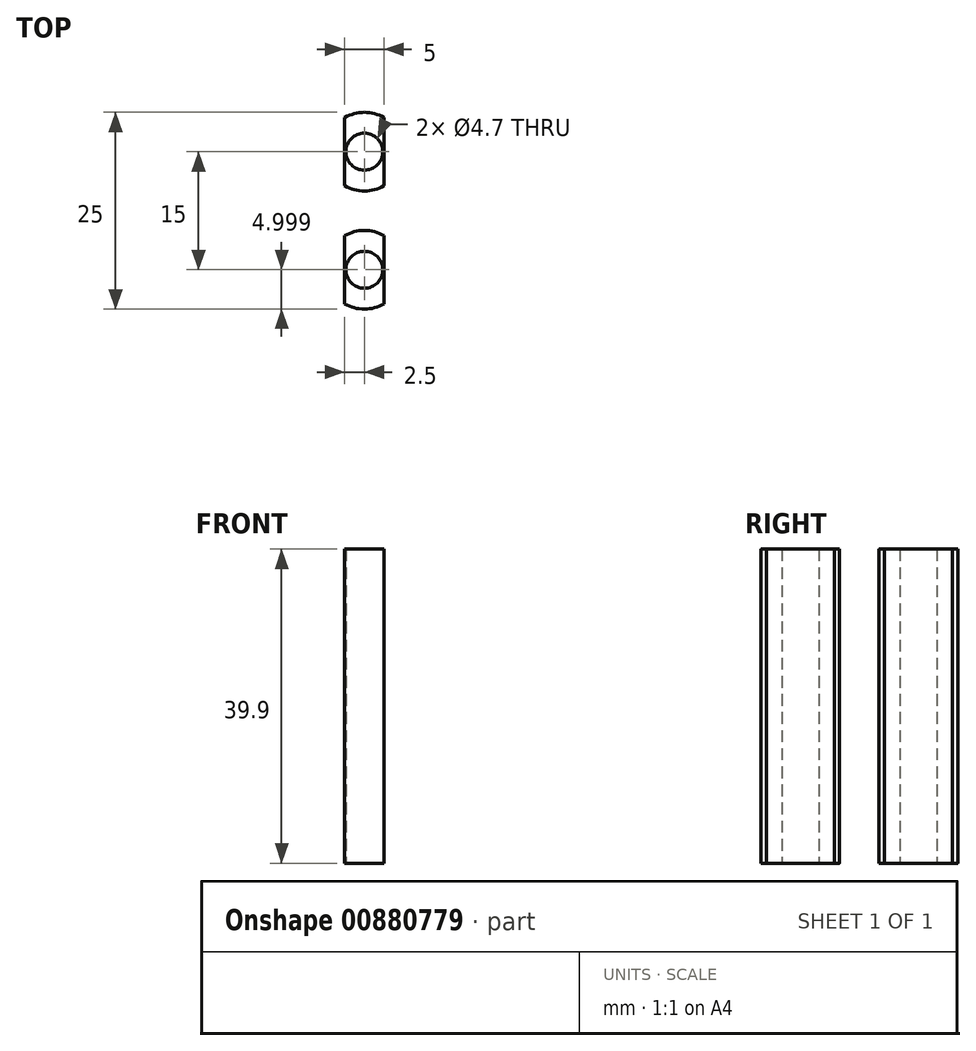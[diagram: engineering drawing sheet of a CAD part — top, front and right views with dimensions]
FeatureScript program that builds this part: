
annotation { "Feature Type Name" : "Feature", "Feature Type Description" : "" }
export const myFeature = defineFeature(function(context is Context, id is Id, definition is map)
    precondition{}
    {
        {
            var Q0;
            Q0=qCreatedBy(makeId("Top.planeOp"),FACE);
            var sketch = newSketch(context, id + "F0", { "sketchPlane" : qUnion([Q0])});
            skPoint(sketch, "E0.center.orphan", {"position": v(0, 29.96) * mm});
            skArc(sketch, "E1", {"start": v(-32.57, -18.1) * mm, "mid": v(-35.07, -17.43) * mm, "end": v(-37.57, -18.1) * mm});
            skLineSegment(sketch, "E2", {"start": v(-32.57, -22.43) * mm, "end": v(-32.57, -18.1) * mm});
            skLineSegment(sketch, "E3", {"start": v(-32.57, -18.1) * mm, "end": v(-32.57, -26.76) * mm});
            skLineSegment(sketch, "E4", {"start": v(-37.57, -22.43) * mm, "end": v(-37.57, -26.76) * mm});
            skLineSegment(sketch, "E5", {"start": v(-37.57, -26.76) * mm, "end": v(-37.57, -18.1) * mm});
            skArc(sketch, "E6.trimOffspring", {"start": v(-37.57, -26.76) * mm, "mid": v(-35.07, -27.43) * mm, "end": v(-32.57, -26.76) * mm});
            skCircle(sketch, "E7", {"center": v(-35.07, -22.43) * mm, "radius": 2.35 * mm});
            skSolve(sketch);
        }
        {
            var Q0;
            Q0 = qSketchRegion(id + "F0", true);
            extrude(context, id + "F1", {"entities" : qUnion([Q0]), "depth" : 39.9 * mm, "offsetDistance" : 25 * mm});
        }
        {
            var Q0;
            Q0=makeQuery(id+"F1.opExtrude","SWEPT_BODY",BODY,{"disambiguationData":[OSD([sQuery(id+"F0.wireOp",EDGE,"E1"),sQuery(id+"F0.wireOp",EDGE,"E3"),sQuery(id+"F0.wireOp",EDGE,"E5"),sQuery(id+"F0.wireOp",EDGE,"E6.trimOffspring"),sQuery(id+"F0.wireOp",EDGE,"E7")])]});
            transform(context, id + "F2", {"entities" : qUnion([Q0]), "transformType" : TransformType.TRANSLATION_3D, "dx" : 0 * mm, "dy" : 15 * mm, "dz" : 0 * mm, "makeCopy" : true});
        }
    });
